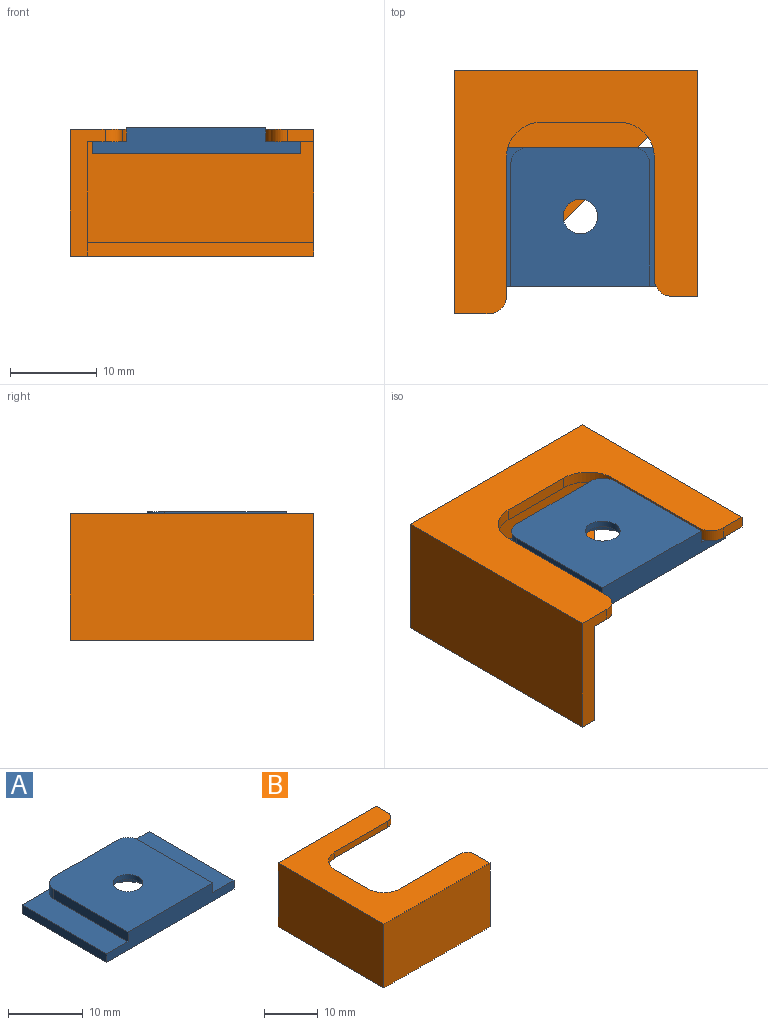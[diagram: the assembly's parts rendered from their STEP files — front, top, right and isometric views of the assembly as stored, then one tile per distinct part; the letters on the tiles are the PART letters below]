
ASSEMBLY  parts=2 mates=1
PART A: 15 faces, bbox 24x16x3 mm
  f0: cylinder r=2mm len=4mm, axis (0,0,-1), area 10.1mm2, adj f10,f11
  f1: plane 16x6mm, normal (0,0,1), area 64.9mm2, adj f2,f3,f5,f8,f14
  f2: plane 16x1.4mm, normal (-1,0,0), area 22.4mm2, adj f1,f3,f5,f7
  f3: plane 24x3mm, normal (0,-1,0), area 59.2mm2, adj f1,f2,f4,f6,f7,f8,f9,f10
  f4: plane 16x1.4mm, normal (1,0,0), area 22.4mm2, adj f3,f5,f6,f7
  f5: plane 24x3mm, normal (0,1,0), area 52.8mm2, adj f1,f2,f4,f6,f7,f10,f13,f14
  f6: plane 16x6mm, normal (0,0,1), area 64.9mm2, adj f3,f4,f5,f9,f13
  f7: plane 24x16mm, normal (0,0,-1), area 320.4mm2, adj f2,f3,f4,f5,f12
  f8: plane 14x1.6mm, normal (-1,0,0), area 22.4mm2, adj f1,f3,f10,f14
  f9: plane 14x1.6mm, normal (1,0,0), area 22.4mm2, adj f3,f6,f10,f13
  f10: plane 16x16mm, normal (0,0,1), area 241.7mm2, adj f0,f3,f5,f8,f9,f13,f14
  f11: plane 9x9mm, normal (0,0,-1), area 51.1mm2, adj f0,f12
  f12: cylinder r=4.5mm len=9mm, axis (0,0,-1), area 62.2mm2, adj f7,f11
  f13: cylinder r=2mm len=2mm, axis (0,0,1), area 5mm2, adj f5,f6,f9,f10
  f14: cylinder r=2mm len=2mm, axis (0,0,-1), area 5mm2, adj f1,f5,f8,f10
PART B: 19 faces, bbox 28x28x14.6 mm
  f0: plane 26x26mm, normal (0.71,0.71,0), area 58.8mm2, adj f2,f3,f7,f8
  f1: plane 28x14.6mm, normal (-1,0,0), area 408.8mm2, adj f2,f4,f8,f13
  f2: plane 28x28mm, normal (0,0,-1), area 446mm2, adj f0,f1,f4,f7,f8
  f3: plane 26x26mm, normal (0,0,1), area 338mm2, adj f0,f5,f6
  f4: plane 28x14.6mm, normal (0,-1,0), area 408.8mm2, adj f1,f2,f7,f13
  f5: plane 26x11.6mm, normal (1,0,0), area 301.6mm2, adj f3,f6,f8,f14
  f6: plane 26x11.6mm, normal (0,1,0), area 301.6mm2, adj f3,f5,f7,f14
  f7: plane 14.6x4mm, normal (1,0,0), area 32mm2, adj f0,f2,f4,f6,f13,f14,f17
  f8: plane 26x14.6mm, normal (0,1,0), area 62.8mm2, adj f0,f1,f2,f5,f9,f13,f14
  f9: plane 3x1.4mm, normal (1,0,0), area 4.2mm2, adj f8,f13,f14,f18
  f10: plane 16x1.4mm, normal (0,1,0), area 22.4mm2, adj f13,f14,f15,f17
  f11: plane 9x1.4mm, normal (1,0,0), area 12.6mm2, adj f13,f14,f15,f16
  f12: plane 14x1.4mm, normal (0,-1,0), area 19.6mm2, adj f13,f14,f16,f18
  f13: plane 28x28mm, normal (0,0,1), area 405.2mm2, adj f1,f4,f7,f8,f9,f10,f11,f12
  f14: plane 26x26mm, normal (0,0,-1), area 297.2mm2, adj f5,f6,f7,f8,f9,f10,f11,f12
  f15: cylinder r=4mm len=4mm, axis (0,0,1), area 8.8mm2, adj f10,f11,f13,f14
  f16: cylinder r=4mm len=4mm, axis (0,0,1), area 8.8mm2, adj f11,f12,f13,f14
  f17: cylinder r=2mm len=2mm, axis (0,0,1), area 4.4mm2, adj f7,f10,f13,f14
  f18: cylinder r=2mm len=2mm, axis (0,0,-1), area 4.4mm2, adj f9,f12,f13,f14
PLACE A t=(-11.98,-7.94,-3.4)mm
PLACE B rot(axis=(0,0,-1),90deg) t=(-14.48,16.9,-15.2)mm
MATE planar B.f14 <-> A.f6  axis (0,0,-1) through (4.52,10.9,-2)mm
